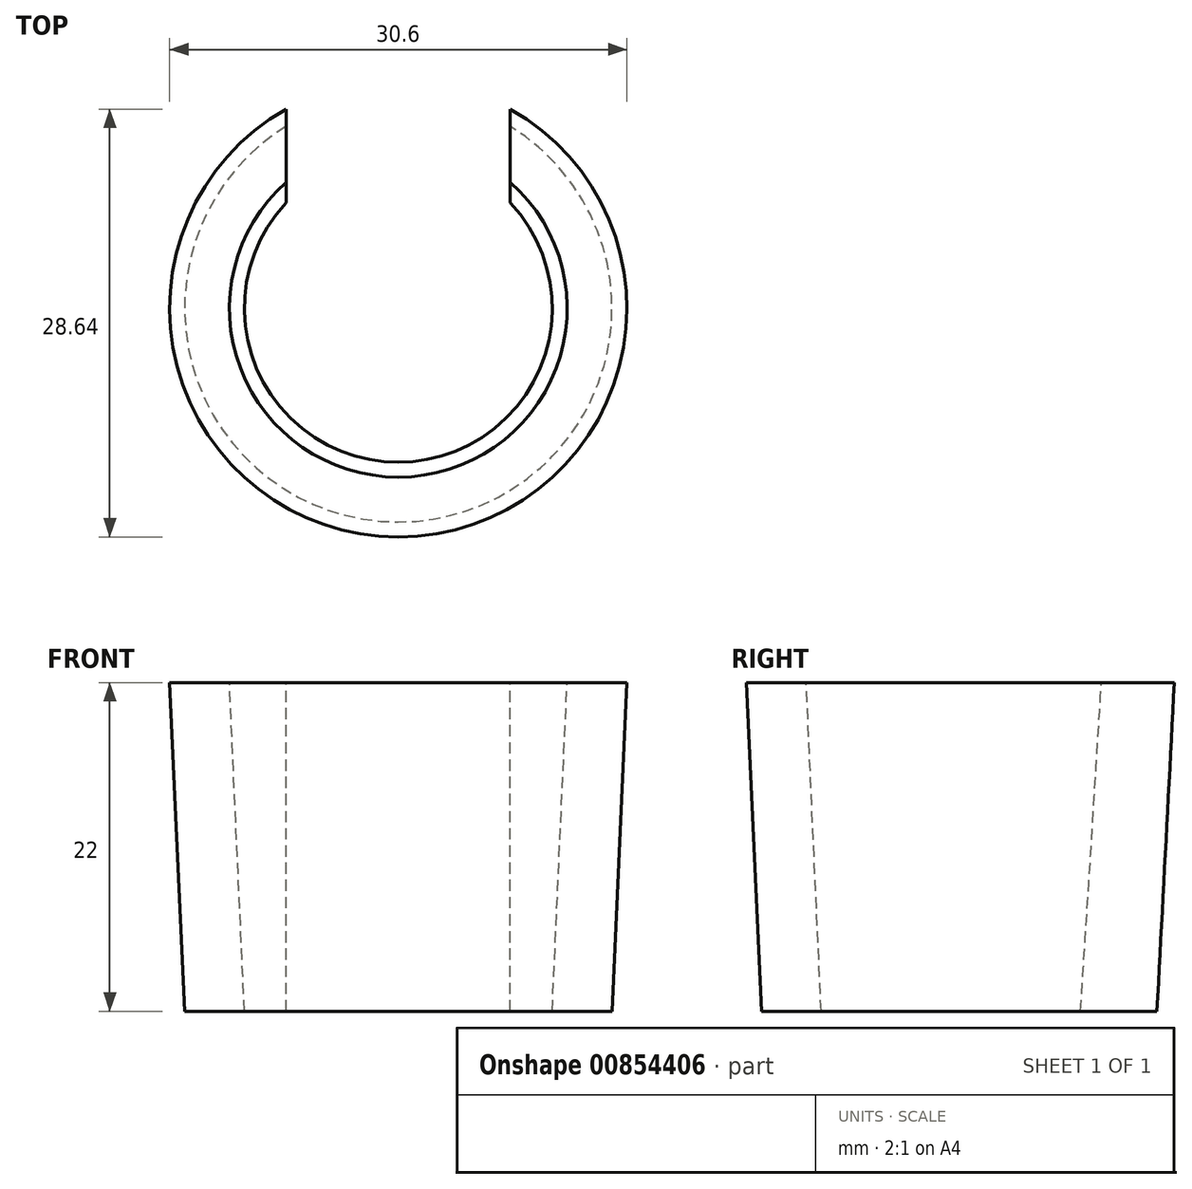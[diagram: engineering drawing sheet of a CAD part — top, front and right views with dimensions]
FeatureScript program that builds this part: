
annotation { "Feature Type Name" : "Feature", "Feature Type Description" : "" }
export const myFeature = defineFeature(function(context is Context, id is Id, definition is map)
    precondition{}
    {
        {
            var Q0;
            Q0=qCreatedBy(makeId("Front.planeOp"),FACE);
            var sketch = newSketch(context, id + "F0", { "sketchPlane" : qUnion([Q0])});
            skLineSegment(sketch, "E0", {"start": v(0, 0) * mm, "end": v(10.3, 0) * mm, "construction": true});
            skLineSegment(sketch, "E1", {"start": v(0, 22) * mm, "end": v(11.3, 22) * mm, "construction": true});
            skLineSegment(sketch, "E2", {"start": v(11.3, 22) * mm, "end": v(10.3, 0) * mm});
            skLineSegment(sketch, "E3", {"start": v(11.3, 22) * mm, "end": v(15.3, 22) * mm});
            skLineSegment(sketch, "E4", {"start": v(10.3, 0) * mm, "end": v(14.3, 0) * mm});
            skLineSegment(sketch, "E5", {"start": v(15.3, 22) * mm, "end": v(14.3, 0) * mm});
            skLineSegment(sketch, "E6", {"start": v(0, 22) * mm, "end": v(0, 0) * mm, "construction": true});
            skSolve(sketch);
        }
        {
            var Q0;
            Q0=makeQuery(id+"F0.imprint","IMPRINT",FACE,{"disambiguationData":[TD([[makeQuery(id+"F0.imprint","IMPRINT",EDGE,{"derivedFrom":sQuery(id+"F0.wireOp",EDGE,"E2")}),1.0]])]});
            var Q1;
            Q1=sQuery(id+"F0.wireOp",EDGE,"E6");
            revolve(context, id + "F1", {"surfaceOperationType" : NewSurfaceOperationType.NEW, "entities" : qUnion([Q0]), "axis" : qUnion([Q1]), "revolveType" : RevolveType.FULL});
        }
        {
            var Q0;
            Q0=qCreatedBy(makeId("Front.planeOp"),FACE);
            var sketch = newSketch(context, id + "F2", { "sketchPlane" : qUnion([Q0])});
            skLineSegment(sketch, "E7.bottom", {"start": v(-7.5, 24.84) * mm, "end": v(7.5, 24.84) * mm});
            skLineSegment(sketch, "E7.top", {"start": v(-7.5, 0) * mm, "end": v(7.5, 0) * mm});
            skLineSegment(sketch, "E7.left", {"start": v(-7.5, 24.84) * mm, "end": v(-7.5, 0) * mm});
            skLineSegment(sketch, "E7.right", {"start": v(7.5, 24.84) * mm, "end": v(7.5, 0) * mm});
            skSolve(sketch);
        }
        {
            var Q0;
            Q0=makeQuery(id+"F2.imprint","IMPRINT",FACE,{"disambiguationData":[TD([[makeQuery(id+"F2.imprint","IMPRINT",EDGE,{"derivedFrom":sQuery(id+"F2.wireOp",EDGE,"E7.bottom")}),-1.0]])]});
            extrude(context, id + "F3", {"entities" : qUnion([Q0]), "operationType" : NewBodyOperationType.REMOVE, "oppositeDirection" : true, "depth" : 25 * mm, "offsetDistance" : 25 * mm});
        }
    });
